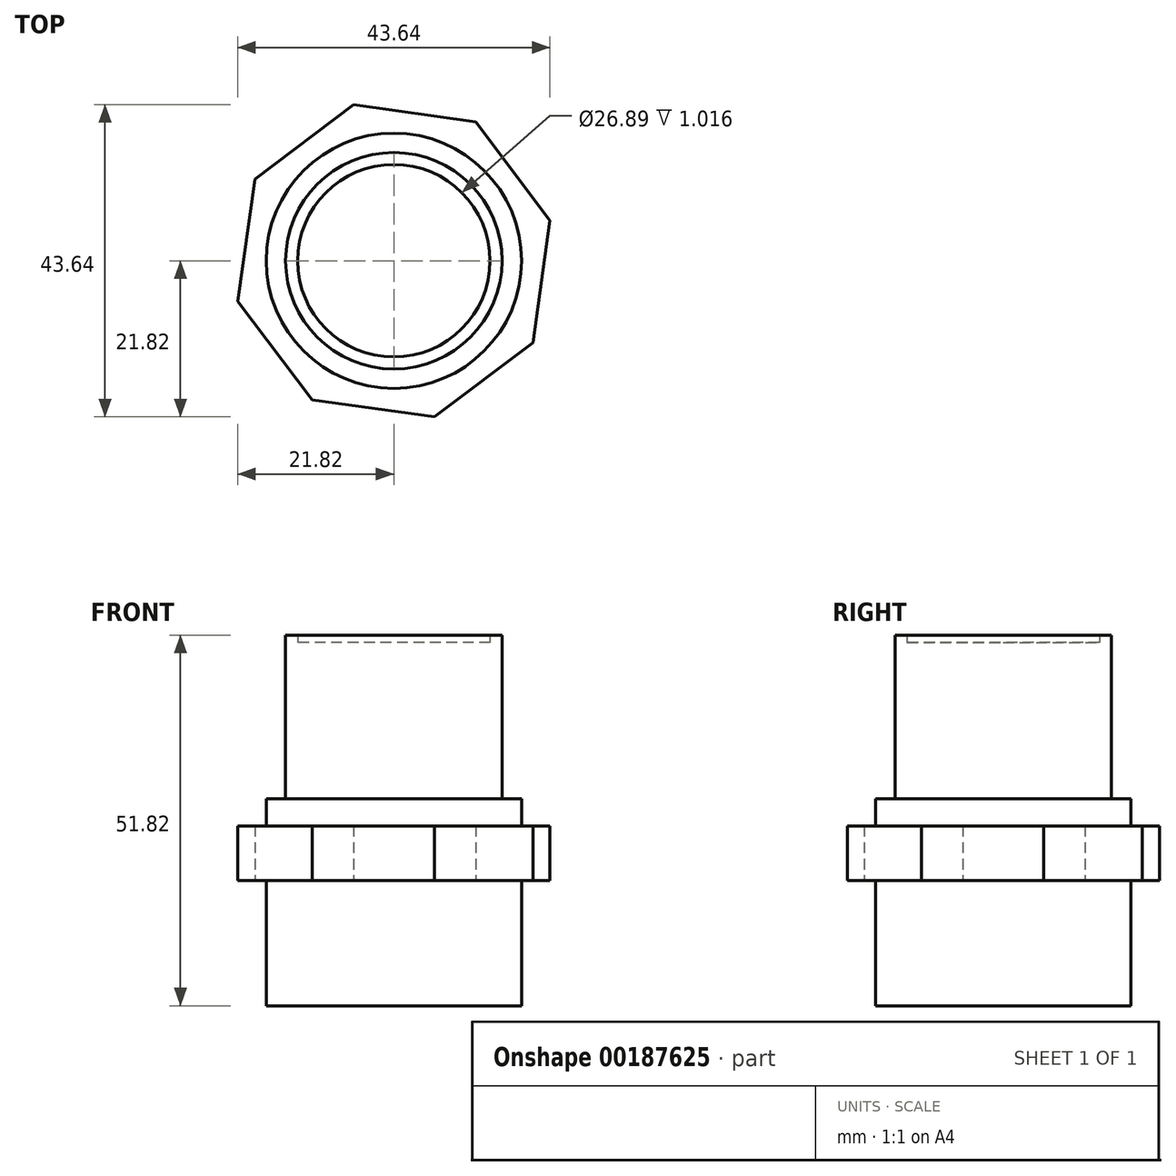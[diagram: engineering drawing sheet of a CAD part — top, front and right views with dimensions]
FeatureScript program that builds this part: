
annotation { "Feature Type Name" : "Feature", "Feature Type Description" : "" }
export const myFeature = defineFeature(function(context is Context, id is Id, definition is map)
    precondition{}
    {
        {
            var Q0;
            Q0=qCreatedBy(makeId("Top.planeOp"),FACE);
            var sketch = newSketch(context, id + "F0", { "sketchPlane" : qUnion([Q0])});
            skCircle(sketch, "E0", {"center": v(0, 0) * mm, "radius": 15.13 * mm});
            skCircle(sketch, "E1", {"center": v(0, 0) * mm, "radius": 13.45 * mm});
            skCircle(sketch, "E2", {"center": v(0, 0) * mm, "radius": 17.84 * mm});
            skCircle(sketch, "E3.cCircle", {"center": v(0, 0) * mm, "radius": 22.54 * mm, "construction": true});
            skLineSegment(sketch, "E3.0", {"start": v(11.43, 19.42) * mm, "end": v(21.82, 5.65) * mm});
            skLineSegment(sketch, "E3.1", {"start": v(21.82, 5.65) * mm, "end": v(19.42, -11.43) * mm});
            skLineSegment(sketch, "E3.2", {"start": v(19.42, -11.43) * mm, "end": v(5.65, -21.82) * mm});
            skLineSegment(sketch, "E3.3", {"start": v(5.65, -21.82) * mm, "end": v(-11.43, -19.42) * mm});
            skLineSegment(sketch, "E3.4", {"start": v(-11.43, -19.42) * mm, "end": v(-21.82, -5.65) * mm});
            skLineSegment(sketch, "E3.5", {"start": v(-21.82, -5.65) * mm, "end": v(-19.42, 11.43) * mm});
            skLineSegment(sketch, "E3.6", {"start": v(-19.42, 11.43) * mm, "end": v(-5.65, 21.82) * mm});
            skLineSegment(sketch, "E3.7", {"start": v(-5.65, 21.82) * mm, "end": v(11.43, 19.42) * mm});
            skSolve(sketch);
        }
        {
            var Q0;
            Q0=makeQuery(id+"F0.imprint","IMPRINT",FACE,{"disambiguationData":[TD([[makeQuery(id+"F0.imprint","IMPRINT",EDGE,{"derivedFrom":sQuery(id+"F0.wireOp",EDGE,"E1")}),1.0]])]});
            extrude(context, id + "F1", {"entities" : qUnion([Q0]), "depth" : 50.8 * mm});
        }
        {
            var Q0;
            Q0=makeQuery(id+"F0.imprint","IMPRINT",FACE,{"disambiguationData":[TD([[makeQuery(id+"F0.imprint","IMPRINT",EDGE,{"derivedFrom":sQuery(id+"F0.wireOp",EDGE,"E0")}),1.0]])]});
            extrude(context, id + "F2", {"entities" : qUnion([Q0]), "operationType" : NewBodyOperationType.ADD, "depth" : 51.82 * mm});
        }
        {
            var Q0;
            Q0=makeQuery(id+"F0.imprint","IMPRINT",FACE,{"disambiguationData":[TD([[makeQuery(id+"F0.imprint","IMPRINT",EDGE,{"derivedFrom":sQuery(id+"F0.wireOp",EDGE,"E0")}),-1.0]])]});
            extrude(context, id + "F3", {"entities" : qUnion([Q0]), "operationType" : NewBodyOperationType.ADD, "depth" : 28.96 * mm});
        }
        {
            var Q0;
            Q0=makeQuery(id+"F0.imprint","IMPRINT",FACE,{"disambiguationData":[TD([[makeQuery(id+"F0.imprint","IMPRINT",EDGE,{"derivedFrom":sQuery(id+"F0.wireOp",EDGE,"E2")}),-1.0]])]});
            extrude(context, id + "F4", {"entities" : qUnion([Q0]), "operationType" : NewBodyOperationType.ADD, "depth" : 25.15 * mm, "hasSecondDirection" : true, "secondDirectionOppositeDirection" : false, "secondDirectionDepth" : 17.53 * mm});
        }
    });
